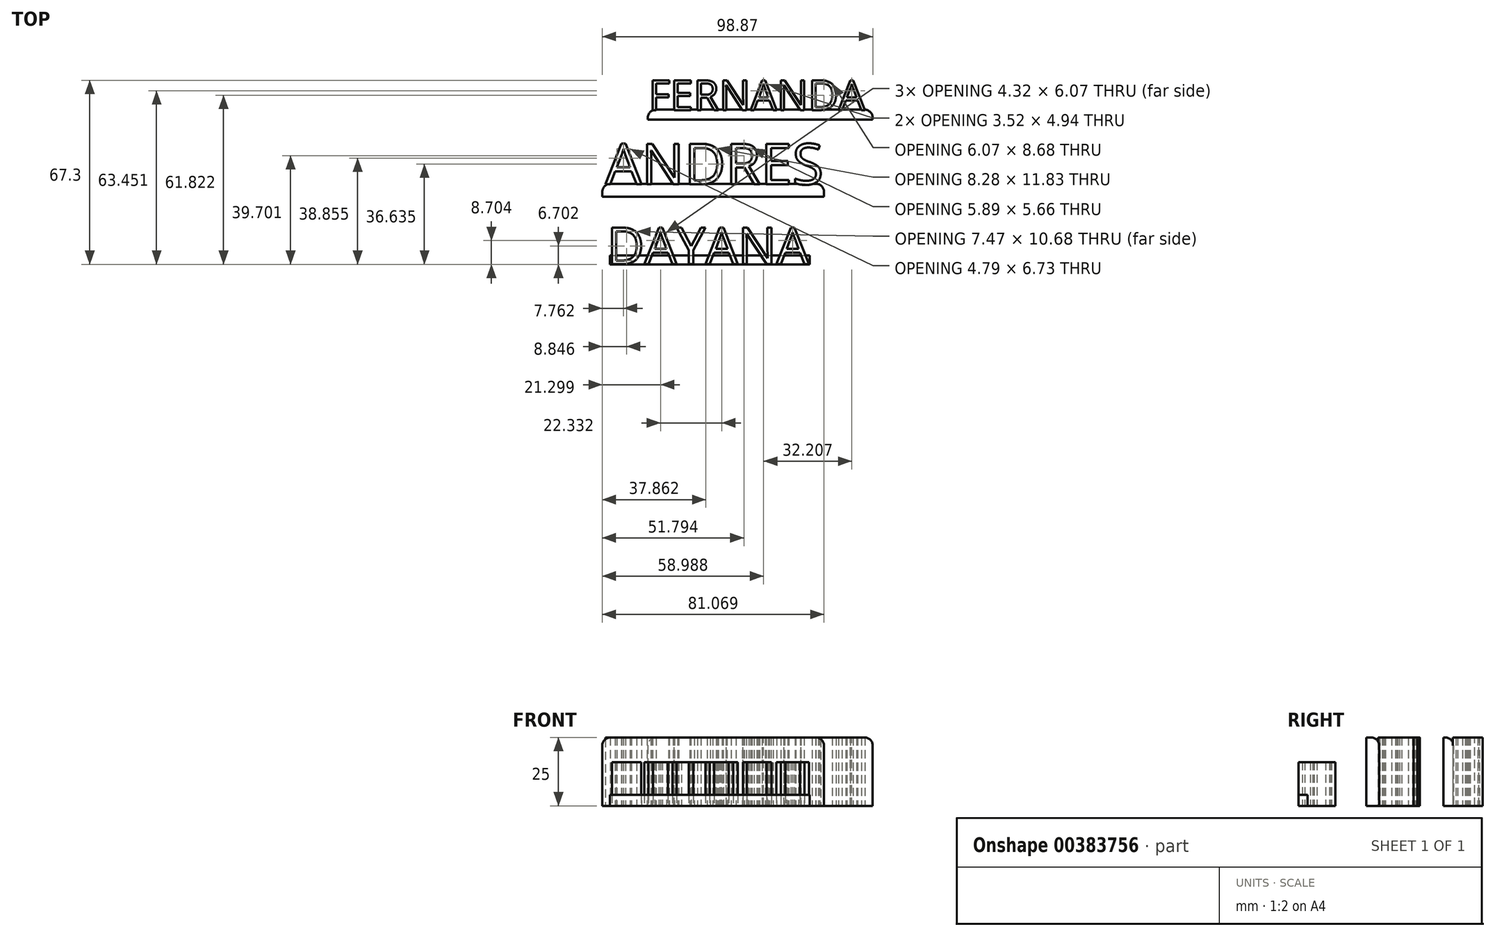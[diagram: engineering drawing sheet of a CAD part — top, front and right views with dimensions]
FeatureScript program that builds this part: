
annotation { "Feature Type Name" : "Feature", "Feature Type Description" : "" }
export const myFeature = defineFeature(function(context is Context, id is Id, definition is map)
    precondition{}
    {
        {
            var Q0;
            Q0=qCreatedBy(makeId("Top.planeOp"),FACE);
            var sketch = newSketch(context, id + "F0", { "sketchPlane" : qUnion([Q0])});
            skText(sketch, "E0", { "text": "FERNANDA", "fontName": "OpenSans-Regular.ttf"});
            const initialGuessF0  = {"E0": [-0.04702, 0.0173, 1, 0, 0.01096]};
            skSetInitialGuess(sketch, initialGuessF0);
            skSolve(sketch);
        }
        {
            var Q0;
            Q0=qCreatedBy(makeId("Top.planeOp"),FACE);
            var sketch = newSketch(context, id + "F1", { "sketchPlane" : qUnion([Q0])});
            skLineSegment(sketch, "E1.bottom", {"start": v(-47.35, 17.46) * mm, "end": v(34.89, 17.46) * mm});
            skLineSegment(sketch, "E1.top", {"start": v(-47.35, 13.8) * mm, "end": v(34.89, 13.8) * mm});
            skLineSegment(sketch, "E1.left", {"start": v(-47.35, 17.46) * mm, "end": v(-47.35, 13.8) * mm});
            skLineSegment(sketch, "E1.right", {"start": v(34.89, 17.46) * mm, "end": v(34.89, 13.8) * mm});
            skSolve(sketch);
        }
        {
            var Q0;
            Q0 = qSketchRegion(id + "F0", true);
            var Q1;
            Q1 = qSketchRegion(id + "F1", true);
            extrude(context, id + "F2", {"entities" : qUnion([Q0, Q1]), "depth" : 25 * mm});
        }
        {
            var Q0;
            Q0=makeQuery(id+"F2.opExtrude","SWEPT_EDGE",EDGE,{"disambiguationData":[OSD([sQuery(id+"F1.wireOp",EDGE,"E1.bottom"),sQuery(id+"F1.wireOp",EDGE,"E1.left")])]});
            fillet(context, id + "F3", {"entities" : qUnion([Q0]), "radius" : 3 * mm, "tangentPropagation" : true, "allowEdgeOverflow" : false});
        }
        {
            var Q0;
            Q0=makeQuery(id+"F2.opExtrude","SWEPT_EDGE",EDGE,{"disambiguationData":[OSD([sQuery(id+"F1.wireOp",EDGE,"E1.bottom"),sQuery(id+"F1.wireOp",EDGE,"E1.right")])]});
            fillet(context, id + "F4", {"entities" : qUnion([Q0]), "radius" : 3 * mm, "tangentPropagation" : true, "allowEdgeOverflow" : false});
        }
        {
            var Q0;
            {var subQ0=sQuery(id+"F1.wireOp",EDGE,"E1.left");var subQ1=sQuery(id+"F1.wireOp",EDGE,"E1.bottom");Q0=makeQuery(id+"F3.opFillet","BLEND_EDGE",EDGE,{"blendedFrom":[makeQuery(id+"F2.opExtrude","SWEPT_EDGE",EDGE,{"disambiguationData":[OSD([subQ1,subQ0])]}),makeQuery(id+"F2.opExtrude","CAP_FACE",FACE,{"disambiguationData":[OSD([subQ1,sQuery(id+"F1.wireOp",EDGE,"E1.top"),subQ0,sQuery(id+"F1.wireOp",EDGE,"E1.right")])],"isStart":false})],"blendedInto":[makeQuery(id+"F2.opExtrude","CAP_FACE",FACE,{"disambiguationData":[OSD([subQ1,sQuery(id+"F1.wireOp",EDGE,"E1.top"),subQ0,sQuery(id+"F1.wireOp",EDGE,"E1.right")])],"isStart":false})]});}
            fillet(context, id + "F5", {"entities" : qUnion([Q0]), "radius" : 3 * mm, "tangentPropagation" : true, "allowEdgeOverflow" : false});
        }
        {
            var Q0;
            Q0=qCreatedBy(makeId("Top.planeOp"),FACE);
            var sketch = newSketch(context, id + "F6", { "sketchPlane" : qUnion([Q0])});
            skText(sketch, "E2", { "text": "ANDRES", "fontName": "OpenSans-Regular.ttf"});
            const initialGuessF6  = {"E2": [-0.06279, -0.00986, 1, 0, 0.01494]};
            skSetInitialGuess(sketch, initialGuessF6);
            skSolve(sketch);
        }
        {
            var Q0;
            Q0=qCreatedBy(makeId("Top.planeOp"),FACE);
            var sketch = newSketch(context, id + "F7", { "sketchPlane" : qUnion([Q0])});
            skLineSegment(sketch, "E3.bottom", {"start": v(-63.98, -9.63) * mm, "end": v(17.08, -9.63) * mm});
            skLineSegment(sketch, "E3.top", {"start": v(-63.98, -14.33) * mm, "end": v(17.08, -14.33) * mm});
            skLineSegment(sketch, "E3.left", {"start": v(-63.98, -9.63) * mm, "end": v(-63.98, -14.33) * mm});
            skLineSegment(sketch, "E3.right", {"start": v(17.08, -9.63) * mm, "end": v(17.08, -14.33) * mm});
            skSolve(sketch);
        }
        {
            var Q0;
            Q0 = qSketchRegion(id + "F6", true);
            var Q1;
            Q1 = qSketchRegion(id + "F7", true);
            extrude(context, id + "F8", {"entities" : qUnion([Q0, Q1]), "depth" : 25 * mm});
        }
        {
            var Q0;
            Q0=makeQuery(id+"F8.opExtrude","SWEPT_EDGE",EDGE,{"disambiguationData":[OSD([sQuery(id+"F7.wireOp",EDGE,"E3.bottom"),sQuery(id+"F7.wireOp",EDGE,"E3.left")])]});
            fillet(context, id + "F9", {"entities" : qUnion([Q0]), "radius" : 3 * mm, "tangentPropagation" : true, "allowEdgeOverflow" : false});
        }
        {
            var Q0;
            Q0=makeQuery(id+"F8.opExtrude","SWEPT_EDGE",EDGE,{"disambiguationData":[OSD([sQuery(id+"F7.wireOp",EDGE,"E3.bottom"),sQuery(id+"F7.wireOp",EDGE,"E3.right")])]});
            fillet(context, id + "F10", {"entities" : qUnion([Q0]), "radius" : 3 * mm, "tangentPropagation" : true, "allowEdgeOverflow" : false});
        }
        {
            var Q0;
            {var subQ0=sQuery(id+"F7.wireOp",EDGE,"E3.left");var subQ1=sQuery(id+"F7.wireOp",EDGE,"E3.bottom");Q0=makeQuery(id+"F9.opFillet","BLEND_EDGE",EDGE,{"blendedFrom":[makeQuery(id+"F8.opExtrude","SWEPT_EDGE",EDGE,{"disambiguationData":[OSD([subQ1,subQ0])]}),makeQuery(id+"F8.opExtrude","CAP_FACE",FACE,{"disambiguationData":[OSD([subQ1,sQuery(id+"F7.wireOp",EDGE,"E3.top"),subQ0,sQuery(id+"F7.wireOp",EDGE,"E3.right")])],"isStart":false})],"blendedInto":[makeQuery(id+"F8.opExtrude","CAP_FACE",FACE,{"disambiguationData":[OSD([subQ1,sQuery(id+"F7.wireOp",EDGE,"E3.top"),subQ0,sQuery(id+"F7.wireOp",EDGE,"E3.right")])],"isStart":false})]});}
            fillet(context, id + "F11", {"entities" : qUnion([Q0]), "radius" : 3 * mm, "tangentPropagation" : true, "allowEdgeOverflow" : false});
        }
        {
            var Q0;
            Q0=qCreatedBy(makeId("Top.planeOp"),FACE);
            var sketch = newSketch(context, id + "F12", { "sketchPlane" : qUnion([Q0])});
            skText(sketch, "E4", { "text": "DAYANA", "fontName": "OpenSans-Regular.ttf"});
            const initialGuessF12  = {"E4": [-0.06226, -0.03907, 1, 0, 0.01348]};
            skSetInitialGuess(sketch, initialGuessF12);
            skSolve(sketch);
        }
        {
            var Q0;
            Q0 = qSketchRegion(id + "F12", true);
            extrude(context, id + "F13", {"entities" : qUnion([Q0]), "depth" : 16 * mm, "offsetDistance" : 25 * mm});
        }
        {
            var Q0;
            Q0=qCreatedBy(makeId("Top.planeOp"),FACE);
            var sketch = newSketch(context, id + "F14", { "sketchPlane" : qUnion([Q0])});
            skLineSegment(sketch, "E5.bottom", {"start": v(-61.24, -35.86) * mm, "end": v(11.86, -35.86) * mm});
            skLineSegment(sketch, "E5.top", {"start": v(-61.24, -39.09) * mm, "end": v(11.86, -39.09) * mm});
            skLineSegment(sketch, "E5.left", {"start": v(-61.24, -35.86) * mm, "end": v(-61.24, -39.09) * mm});
            skLineSegment(sketch, "E5.right", {"start": v(11.86, -35.86) * mm, "end": v(11.86, -39.09) * mm});
            skSolve(sketch);
        }
        {
            var Q0;
            Q0 = qSketchRegion(id + "F14", true);
            extrude(context, id + "F15", {"entities" : qUnion([Q0]), "depth" : 4 * mm, "offsetDistance" : 25 * mm});
        }
    });
